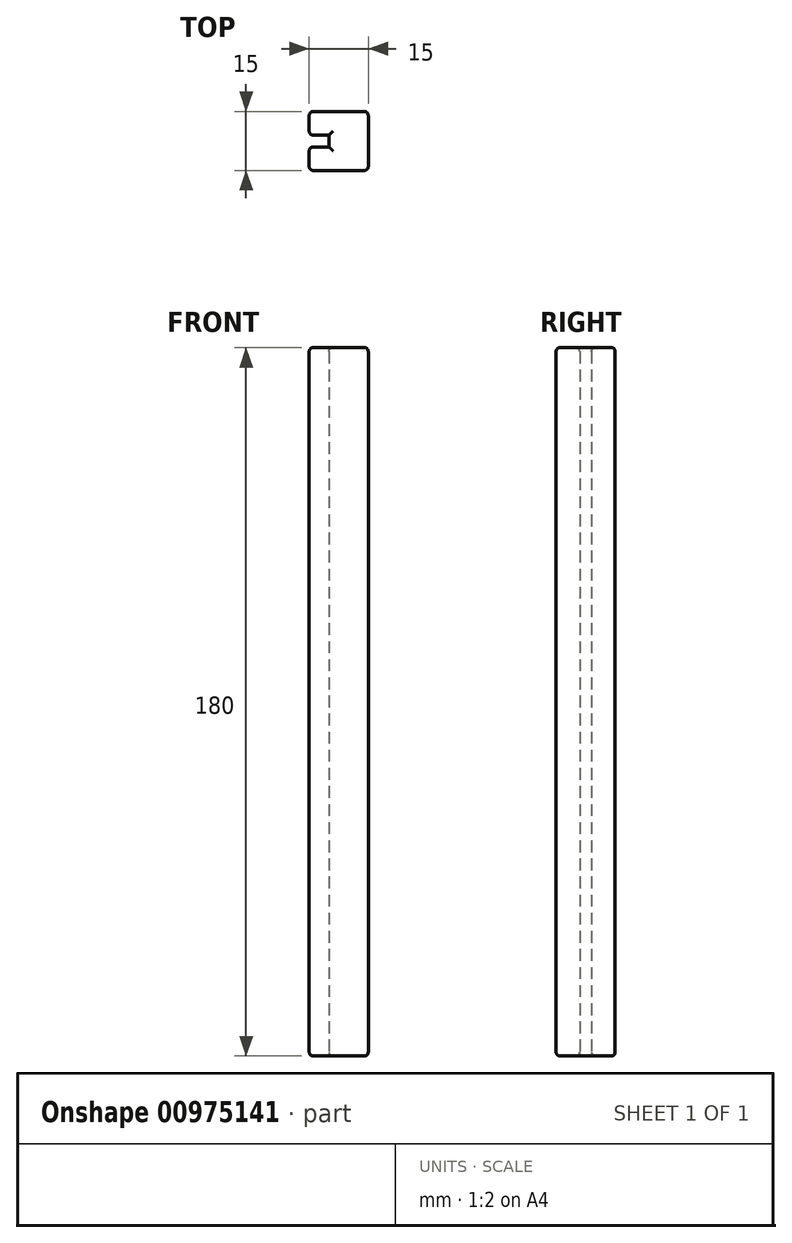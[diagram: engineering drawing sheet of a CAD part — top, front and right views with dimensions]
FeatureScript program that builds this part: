
annotation { "Feature Type Name" : "Feature", "Feature Type Description" : "" }
export const myFeature = defineFeature(function(context is Context, id is Id, definition is map)
    precondition{}
    {
        {
            var Q0;
            Q0=qCreatedBy(makeId("Top.planeOp"),FACE);
            var sketch = newSketch(context, id + "F0", { "sketchPlane" : qUnion([Q0])});
            skLineSegment(sketch, "E0.bottom", {"start": v(-7.5, 7.5) * mm, "end": v(7.5, 7.5) * mm});
            skLineSegment(sketch, "E0.top", {"start": v(-7.5, -7.5) * mm, "end": v(7.5, -7.5) * mm});
            skLineSegment(sketch, "E0.left", {"start": v(-7.5, 7.5) * mm, "end": v(-7.5, 1.5) * mm});
            skLineSegment(sketch, "E0.right", {"start": v(7.5, 7.5) * mm, "end": v(7.5, -7.5) * mm});
            skLineSegment(sketch, "E1.bottom", {"start": v(-7.5, 1.5) * mm, "end": v(-2.5, 1.5) * mm});
            skLineSegment(sketch, "E1.top", {"start": v(-7.5, -1.5) * mm, "end": v(-2.5, -1.5) * mm});
            skLineSegment(sketch, "E1.right", {"start": v(-2.5, 1.5) * mm, "end": v(-2.5, -1.5) * mm});
            skLineSegment(sketch, "E2.trimOffspring", {"start": v(-7.5, -1.5) * mm, "end": v(-7.5, -7.5) * mm});
            skSolve(sketch);
        }
        {
            var Q0;
            Q0=makeQuery(id+"F0.imprint","IMPRINT",FACE,{"disambiguationData":[TD([[makeQuery(id+"F0.imprint","IMPRINT",EDGE,{"derivedFrom":sQuery(id+"F0.wireOp",EDGE,"E0.bottom")}),-1.0]])]});
            extrude(context, id + "F1", {"entities" : qUnion([Q0]), "depth" : 180 * mm, "offsetDistance" : 25 * mm});
        }
        {
            var Q0;
            Q0=makeQuery(id+"F1.opExtrude","CAP_FACE",FACE,{"disambiguationData":[OSD([sQuery(id+"F0.wireOp",EDGE,"E0.bottom"),sQuery(id+"F0.wireOp",EDGE,"E0.top"),sQuery(id+"F0.wireOp",EDGE,"E0.left"),sQuery(id+"F0.wireOp",EDGE,"E0.right"),sQuery(id+"F0.wireOp",EDGE,"E1.bottom"),sQuery(id+"F0.wireOp",EDGE,"E1.top"),sQuery(id+"F0.wireOp",EDGE,"E1.right"),sQuery(id+"F0.wireOp",EDGE,"E2.trimOffspring")])],"isStart":false});
            var Q1;
            Q1=makeQuery(id+"F1.opExtrude","CAP_FACE",FACE,{"disambiguationData":[OSD([sQuery(id+"F0.wireOp",EDGE,"E0.bottom"),sQuery(id+"F0.wireOp",EDGE,"E0.top"),sQuery(id+"F0.wireOp",EDGE,"E0.left"),sQuery(id+"F0.wireOp",EDGE,"E0.right"),sQuery(id+"F0.wireOp",EDGE,"E1.bottom"),sQuery(id+"F0.wireOp",EDGE,"E1.top"),sQuery(id+"F0.wireOp",EDGE,"E1.right"),sQuery(id+"F0.wireOp",EDGE,"E2.trimOffspring")])],"isStart":true});
            var Q2;
            Q2=makeQuery(id+"F1.opExtrude","SWEPT_EDGE",EDGE,{"disambiguationData":[OSD([sQuery(id+"F0.wireOp",EDGE,"E0.bottom"),sQuery(id+"F0.wireOp",EDGE,"E0.right")])]});
            var Q3;
            Q3=makeQuery(id+"F1.opExtrude","SWEPT_EDGE",EDGE,{"disambiguationData":[OSD([sQuery(id+"F0.wireOp",EDGE,"E0.bottom"),sQuery(id+"F0.wireOp",EDGE,"E0.left")])]});
            var Q4;
            Q4=makeQuery(id+"F1.opExtrude","SWEPT_EDGE",EDGE,{"disambiguationData":[OSD([sQuery(id+"F0.wireOp",EDGE,"E0.top"),sQuery(id+"F0.wireOp",EDGE,"E0.right")])]});
            var Q5;
            Q5=makeQuery(id+"F1.opExtrude","SWEPT_FACE",FACE,{"disambiguationData":[OSD([sQuery(id+"F0.wireOp",EDGE,"E2.trimOffspring")])]});
            var Q6;
            Q6=makeQuery(id+"F1.opExtrude","SWEPT_FACE",FACE,{"disambiguationData":[OSD([sQuery(id+"F0.wireOp",EDGE,"E0.left")])]});
            fillet(context, id + "F2", {"entities" : qUnion([Q0, Q1, Q2, Q3, Q4, Q5, Q6]), "radius" : 1 * mm, "tangentPropagation" : true, "allowEdgeOverflow" : false});
        }
    });
